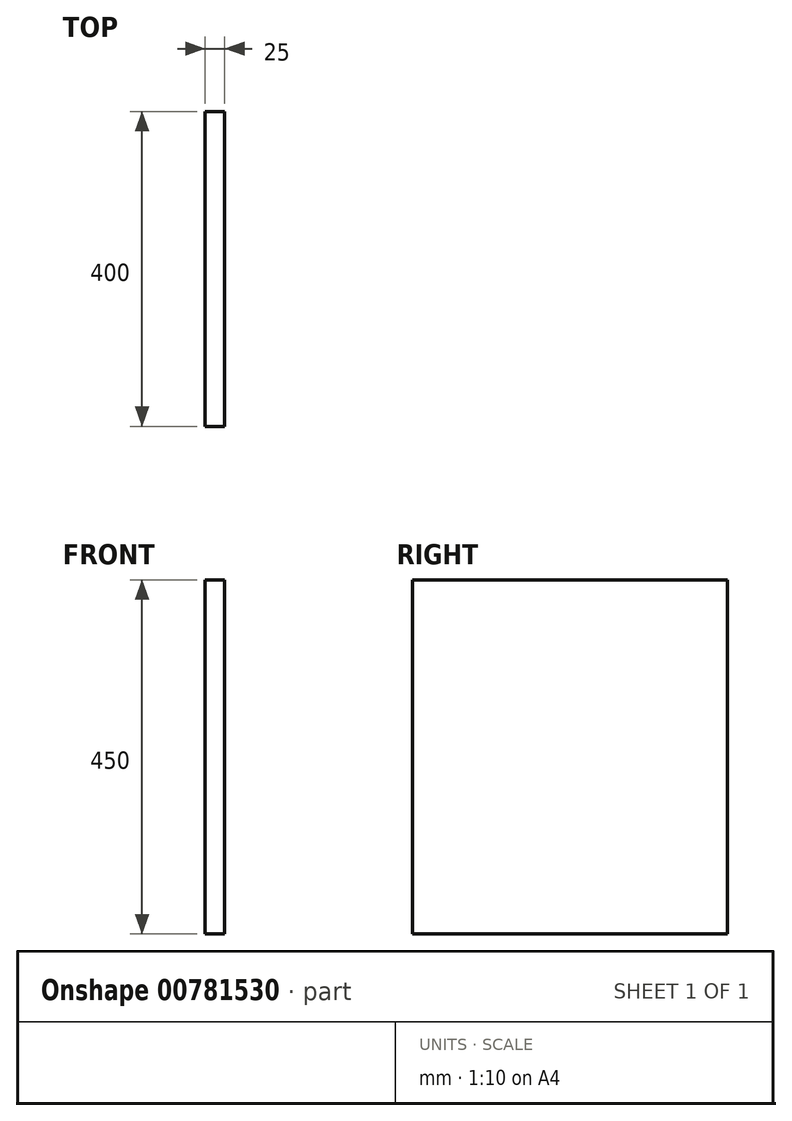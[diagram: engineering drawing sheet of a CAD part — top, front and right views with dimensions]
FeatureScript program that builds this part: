
annotation { "Feature Type Name" : "Feature", "Feature Type Description" : "" }
export const myFeature = defineFeature(function(context is Context, id is Id, definition is map)
    precondition{}
    {
        {
            var Q0;
            Q0=qCreatedBy(makeId("Right.planeOp"),FACE);
            var sketch = newSketch(context, id + "F0", { "sketchPlane" : qUnion([Q0])});
            skLineSegment(sketch, "E0.bottom", {"start": v(0, 0) * mm, "end": v(400, 0) * mm});
            skLineSegment(sketch, "E0.top", {"start": v(0, 450) * mm, "end": v(400, 450) * mm});
            skLineSegment(sketch, "E0.left", {"start": v(0, 0) * mm, "end": v(0, 450) * mm});
            skLineSegment(sketch, "E0.right", {"start": v(400, 0) * mm, "end": v(400, 450) * mm});
            skSolve(sketch);
        }
        {
            var Q0;
            Q0 = qSketchRegion(id + "F0", true);
            extrude(context, id + "F1", {"entities" : qUnion([Q0]), "depth" : 25 * mm, "offsetDistance" : 25 * mm});
        }
    });
